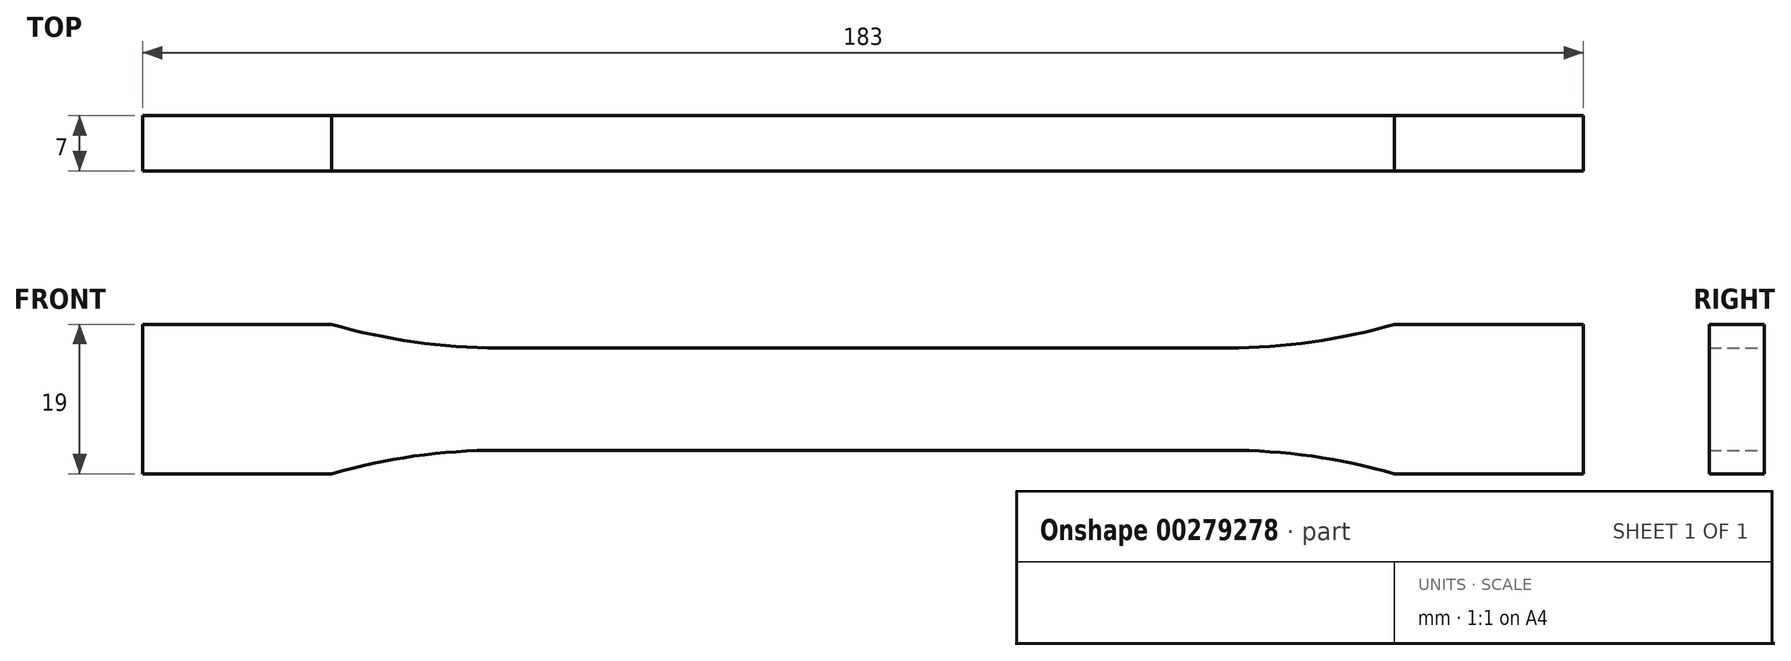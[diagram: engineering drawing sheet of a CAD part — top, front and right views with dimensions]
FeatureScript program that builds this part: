
annotation { "Feature Type Name" : "Feature", "Feature Type Description" : "" }
export const myFeature = defineFeature(function(context is Context, id is Id, definition is map)
    precondition{}
    {
        {
            var Q0;
            Q0=qCreatedBy(makeId("Front.planeOp"),FACE);
            var sketch = newSketch(context, id + "F0", { "sketchPlane" : qUnion([Q0])});
            skLineSegment(sketch, "E0", {"start": v(0, 6.5) * mm, "end": v(46.36, 6.5) * mm});
            skArc(sketch, "E1", {"start": v(46.36, 6.5) * mm, "mid": v(57.03, 7.25) * mm, "end": v(67.5, 9.5) * mm});
            skLineSegment(sketch, "E2", {"start": v(67.5, 9.5) * mm, "end": v(91.5, 9.5) * mm});
            skLineSegment(sketch, "E3.MirrorCS", {"start": v(0, -6.5) * mm, "end": v(46.36, -6.5) * mm});
            skLineSegment(sketch, "E4.MirrorCS", {"start": v(67.5, -9.5) * mm, "end": v(91.5, -9.5) * mm});
            skArc(sketch, "E5.MirrorCS", {"start": v(46.36, -6.5) * mm, "mid": v(57.03, -7.25) * mm, "end": v(67.5, -9.5) * mm});
            skLineSegment(sketch, "E6.MirrorCS", {"start": v(-67.5, 9.5) * mm, "end": v(-91.5, 9.5) * mm});
            skLineSegment(sketch, "E7.MirrorCS", {"start": v(-67.5, -9.5) * mm, "end": v(-91.5, -9.5) * mm});
            skArc(sketch, "E8.MirrorCS", {"start": v(-46.36, -6.5) * mm, "mid": v(-57.03, -7.25) * mm, "end": v(-67.5, -9.5) * mm});
            skLineSegment(sketch, "E9.MirrorCS", {"start": v(0, -6.5) * mm, "end": v(-46.36, -6.5) * mm});
            skLineSegment(sketch, "E10.MirrorCS", {"start": v(0, 6.5) * mm, "end": v(-46.36, 6.5) * mm});
            skArc(sketch, "E11.MirrorCS", {"start": v(-46.36, 6.5) * mm, "mid": v(-57.03, 7.25) * mm, "end": v(-67.5, 9.5) * mm});
            skLineSegment(sketch, "E12", {"start": v(-91.5, 9.5) * mm, "end": v(-91.5, -9.5) * mm});
            skLineSegment(sketch, "E13", {"start": v(91.5, 9.5) * mm, "end": v(91.5, -9.5) * mm});
            skSolve(sketch);
        }
        {
            var Q0;
            Q0 = qSketchRegion(id + "F0", true);
            extrude(context, id + "F1", {"entities" : qUnion([Q0]), "depth" : 7 * mm});
        }
    });
